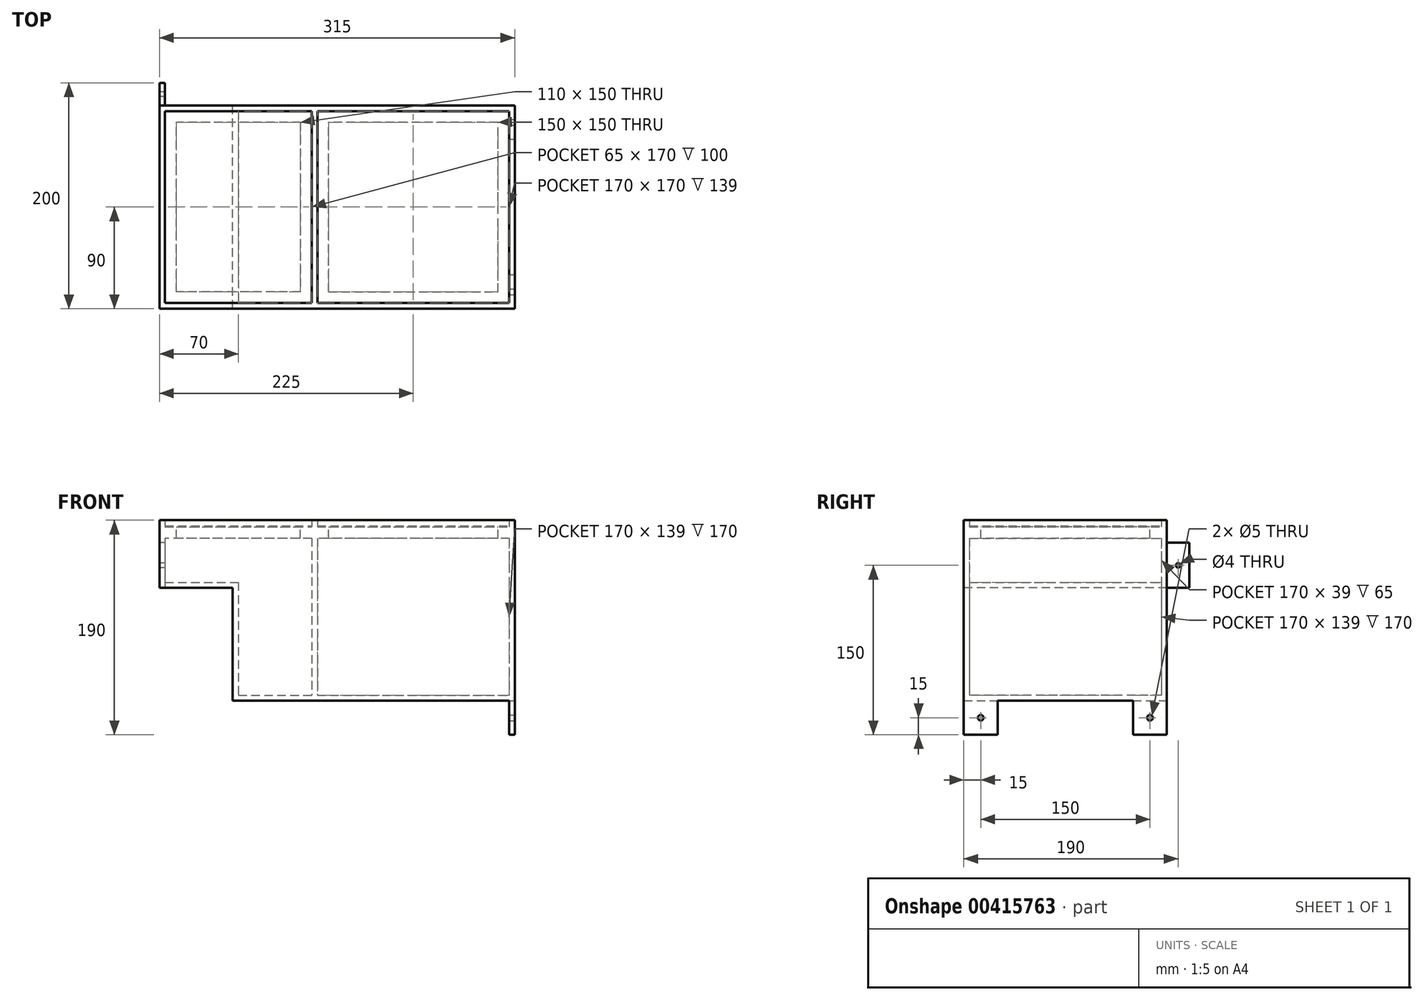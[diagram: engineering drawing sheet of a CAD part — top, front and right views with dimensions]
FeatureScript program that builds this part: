
annotation { "Feature Type Name" : "Feature", "Feature Type Description" : "" }
export const myFeature = defineFeature(function(context is Context, id is Id, definition is map)
    precondition{}
    {
        {
            var Q0;
            Q0=qCreatedBy(makeId("Top.planeOp"),FACE);
            var sketch = newSketch(context, id + "F0", { "sketchPlane" : qUnion([Q0])});
            skLineSegment(sketch, "E0.bottom", {"start": v(125, -90) * mm, "end": v(-125, -90) * mm});
            skLineSegment(sketch, "E0.top", {"start": v(125, 90) * mm, "end": v(-125, 90) * mm});
            skLineSegment(sketch, "E0.left", {"start": v(125, -90) * mm, "end": v(125, 90) * mm});
            skLineSegment(sketch, "E0.right", {"start": v(-125, -90) * mm, "end": v(-125, 90) * mm});
            skPoint(sketch, "E0.middle", {"position": v(0, 0) * mm});
            skLineSegment(sketch, "E1", {"start": v(-55, 90) * mm, "end": v(-55, -90) * mm});
            skLineSegment(sketch, "E2", {"start": v(-50, 90) * mm, "end": v(-50, -90) * mm});
            skLineSegment(sketch, "E3", {"start": v(-125, 85) * mm, "end": v(125, 85) * mm});
            skLineSegment(sketch, "E4", {"start": v(125, -85) * mm, "end": v(-125, -85) * mm});
            skLineSegment(sketch, "E5", {"start": v(120, 85) * mm, "end": v(120, -85) * mm});
            skLineSegment(sketch, "E6", {"start": v(-120, 85) * mm, "end": v(-120, -85) * mm});
            skSolve(sketch);
        }
        {
            var Q0;
            Q0 = qSketchRegion(id + "F0", true);
            var Q1;
            {var subQ0=sQuery(id+"F0.wireOp",EDGE,"E3");var subQ1=sQuery(id+"F0.wireOp",EDGE,"E1");var subQ2=makeQuery(id+"F0.imprint","INTERSECT",VERTEX,{"derivedFrom":[subQ1,subQ0]});Q1=makeQuery(id+"F0.imprint","IMPRINT",FACE,{"disambiguationData":[TD([[makeQuery(id+"F0.imprint","IMPRINT",EDGE,{"disambiguationData":[TD([[subQ2,-1.0]])],"derivedFrom":subQ1}),1.0]])]});}
            extrude(context, id + "F1", {"entities" : qUnion([Q0, Q1]), "depth" : 160 * mm});
        }
        {
            var Q0;
            {var subQ5=sQuery(id+"F0.wireOp",EDGE,"E6");Q0=makeQuery(id+"F0.imprint","IMPRINT",FACE,{"disambiguationData":[TD([[makeQuery(id+"F0.imprint","IMPRINT",EDGE,{"derivedFrom":subQ5}),1.0]])]});}
            var Q1;
            {var subQ5=sQuery(id+"F0.wireOp",EDGE,"E5");Q1=makeQuery(id+"F0.imprint","IMPRINT",FACE,{"disambiguationData":[TD([[makeQuery(id+"F0.imprint","IMPRINT",EDGE,{"derivedFrom":subQ5}),-1.0]])]});}
            extrude(context, id + "F2", {"entities" : qUnion([Q0, Q1]), "operationType" : NewBodyOperationType.ADD, "depth" : 5 * mm});
        }
        {
            var Q0;
            Q0=makeQuery(id+"F1.opExtrude","SWEPT_FACE",FACE,{"disambiguationData":[OSD([sQuery(id+"F0.wireOp",EDGE,"E0.right")])]});
            var sketch = newSketch(context, id + "F3", { "sketchPlane" : qUnion([Q0])});
            skLineSegment(sketch, "E7.bottom", {"start": v(-90, 160) * mm, "end": v(90, 160) * mm});
            skLineSegment(sketch, "E7.top", {"start": v(-90, 100) * mm, "end": v(90, 100) * mm});
            skLineSegment(sketch, "E7.left", {"start": v(-90, 160) * mm, "end": v(-90, 100) * mm});
            skLineSegment(sketch, "E7.right", {"start": v(90, 160) * mm, "end": v(90, 100) * mm});
            skLineSegment(sketch, "E8", {"start": v(90, 155) * mm, "end": v(-90, 155) * mm});
            skLineSegment(sketch, "E9", {"start": v(-90, 105) * mm, "end": v(90, 105) * mm});
            skLineSegment(sketch, "E10", {"start": v(85, 155) * mm, "end": v(85, 105) * mm});
            skLineSegment(sketch, "E11", {"start": v(-85, 155) * mm, "end": v(-85, 105) * mm});
            skSolve(sketch);
        }
        {
            var Q0;
            Q0 = qSketchRegion(id + "F3", true);
            var Q1;
            {var subQ0=sQuery(id+"F3.wireOp",EDGE,"E10");Q1=makeQuery(id+"F3.imprint","IMPRINT",FACE,{"disambiguationData":[TD([[makeQuery(id+"F3.imprint","IMPRINT",EDGE,{"derivedFrom":subQ0}),-1.0]])]});}
            extrude(context, id + "F4", {"entities" : qUnion([Q0, Q1]), "operationType" : NewBodyOperationType.ADD, "depth" : 65 * mm});
        }
        {
            var Q0;
            {var subQ0=sQuery(id+"F3.wireOp",EDGE,"E10");Q0=makeQuery(id+"F3.imprint","IMPRINT",FACE,{"disambiguationData":[TD([[makeQuery(id+"F3.imprint","IMPRINT",EDGE,{"derivedFrom":subQ0}),-1.0]])]});}
            extrude(context, id + "F5", {"entities" : qUnion([Q0]), "operationType" : NewBodyOperationType.REMOVE, "depth" : 60 * mm});
        }
        {
            var Q0;
            {var subQ0=sQuery(id+"F3.wireOp",EDGE,"E10");Q0=makeQuery(id+"F3.imprint","IMPRINT",FACE,{"disambiguationData":[TD([[makeQuery(id+"F3.imprint","IMPRINT",EDGE,{"derivedFrom":subQ0}),-1.0]])]});}
            extrude(context, id + "F6", {"entities" : qUnion([Q0]), "operationType" : NewBodyOperationType.REMOVE, "oppositeDirection" : true, "depth" : 6 * mm});
        }
        {
            var Q0;
            {var subQ0=sQuery(id+"F0.wireOp",EDGE,"E6");Q0=makeQuery(id+"F6.boolean.opBoolean","SPLIT",FACE,{"disambiguationData":[TD([makeQuery(id+"F4.opExtrude","SWEPT_FACE",FACE,{"disambiguationData":[OSD([sQuery(id+"F3.wireOp",EDGE,"E7.bottom")])]})])],"derivedFrom":makeQuery(id+"F1.opExtrude","SWEPT_FACE",FACE,{"disambiguationData":[OSD([subQ0])]})});}
            extrude(context, id + "F7", {"entities" : qUnion([Q0]), "operationType" : NewBodyOperationType.REMOVE, "oppositeDirection" : true, "depth" : 65 * mm});
        }
        {
            var Q0;
            Q0=makeQuery(id+"F4.opExtrude","CAP_FACE",FACE,{"disambiguationData":[OSD([sQuery(id+"F3.wireOp",EDGE,"E7.bottom"),sQuery(id+"F3.wireOp",EDGE,"E7.top"),sQuery(id+"F3.wireOp",EDGE,"E7.left"),sQuery(id+"F3.wireOp",EDGE,"E7.right")])],"isStart":false});
            var sketch = newSketch(context, id + "F8", { "sketchPlane" : qUnion([Q0])});
            skLineSegment(sketch, "E12.bottom", {"start": v(-90, 100) * mm, "end": v(-110, 100) * mm});
            skLineSegment(sketch, "E12.top", {"start": v(-90, 140) * mm, "end": v(-110, 140) * mm});
            skLineSegment(sketch, "E12.left", {"start": v(-90, 100) * mm, "end": v(-90, 140) * mm});
            skLineSegment(sketch, "E12.right", {"start": v(-110, 100) * mm, "end": v(-110, 140) * mm});
            skLineSegment(sketch, "E13", {"start": v(-110, 120) * mm, "end": v(-90, 120) * mm, "construction": true});
            skCircle(sketch, "E14", {"center": v(-100, 120) * mm, "radius": 2 * mm});
            skSolve(sketch);
        }
        {
            var Q0;
            Q0 = qSketchRegion(id + "F8", true);
            extrude(context, id + "F9", {"entities" : qUnion([Q0]), "oppositeDirection" : true, "depth" : 5 * mm});
        }
        {
            var Q0;
            Q0=makeQuery(id+"F1.opExtrude","SWEPT_FACE",FACE,{"disambiguationData":[OSD([sQuery(id+"F0.wireOp",EDGE,"E0.left")])]});
            var sketch = newSketch(context, id + "F10", { "sketchPlane" : qUnion([Q0])});
            skLineSegment(sketch, "E15.bottom", {"start": v(-90, 0) * mm, "end": v(-60, 0) * mm});
            skLineSegment(sketch, "E15.top", {"start": v(-90, -30) * mm, "end": v(-60, -30) * mm});
            skLineSegment(sketch, "E15.left", {"start": v(-90, 0) * mm, "end": v(-90, -30) * mm});
            skLineSegment(sketch, "E15.right", {"start": v(-60, 0) * mm, "end": v(-60, -30) * mm});
            skLineSegment(sketch, "E16.bottom", {"start": v(90, 0) * mm, "end": v(60, 0) * mm});
            skLineSegment(sketch, "E16.top", {"start": v(90, -30) * mm, "end": v(60, -30) * mm});
            skLineSegment(sketch, "E16.left", {"start": v(90, 0) * mm, "end": v(90, -30) * mm});
            skLineSegment(sketch, "E16.right", {"start": v(60, 0) * mm, "end": v(60, -30) * mm});
            skLineSegment(sketch, "E17", {"start": v(-60, -15) * mm, "end": v(-90, -15) * mm, "construction": true});
            skLineSegment(sketch, "E18", {"start": v(90, -15) * mm, "end": v(60, -15) * mm, "construction": true});
            skCircle(sketch, "E19", {"center": v(-75, -15) * mm, "radius": 2.5 * mm});
            skCircle(sketch, "E20", {"center": v(75, -15) * mm, "radius": 2.5 * mm});
            skSolve(sketch);
        }
        {
            var Q0;
            Q0 = qSketchRegion(id + "F10", true);
            extrude(context, id + "F11", {"entities" : qUnion([Q0]), "operationType" : NewBodyOperationType.ADD, "oppositeDirection" : true, "depth" : 5 * mm});
        }
        {
            var Q0;
            {var subQ0=sQuery(id+"F0.wireOp",EDGE,"E3");Q0=makeQuery(id+"F1.opExtrude","SWEPT_FACE",FACE,{"disambiguationData":[OSD([subQ0]),TDD([makeQuery(id+"F0.imprint","IMPRINT",EDGE,{"disambiguationData":[TD([[makeQuery(id+"F0.imprint","INTERSECT",VERTEX,{"derivedFrom":[subQ0,sQuery(id+"F0.wireOp",EDGE,"E5")]}),1.0]])],"derivedFrom":subQ0})])]});}
            var sketch = newSketch(context, id + "F12", { "sketchPlane" : qUnion([Q0])});
            skLineSegment(sketch, "E21", {"start": v(-50, 154) * mm, "end": v(120, 154) * mm});
            skLineSegment(sketch, "E22", {"start": v(120, 144) * mm, "end": v(-50, 144) * mm});
            skSolve(sketch);
        }
        {
            var Q0;
            {var subQ0=sQuery(id+"F12.wireOp",EDGE,"E21");Q0=makeQuery(id+"F12.imprint","IMPRINT",FACE,{"disambiguationData":[TD([[makeQuery(id+"F12.imprint","IMPRINT",EDGE,{"derivedFrom":subQ0}),-1.0]])]});}
            extrude(context, id + "F13", {"entities" : qUnion([Q0]), "operationType" : NewBodyOperationType.ADD, "depth" : 170 * mm});
        }
        {
            var Q0;
            Q0=makeQuery(id+"F13.opExtrude","SWEPT_FACE",FACE,{"disambiguationData":[OSD([sQuery(id+"F12.wireOp",EDGE,"E21")])]});
            var sketch = newSketch(context, id + "F14", { "sketchPlane" : qUnion([Q0])});
            skLineSegment(sketch, "E23", {"start": v(-50, 75) * mm, "end": v(120, 75) * mm});
            skLineSegment(sketch, "E24", {"start": v(120, -75) * mm, "end": v(-50, -75) * mm});
            skLineSegment(sketch, "E25", {"start": v(110, 75) * mm, "end": v(110, -75) * mm});
            skLineSegment(sketch, "E26", {"start": v(-40, 75) * mm, "end": v(-40, -75) * mm});
            skSolve(sketch);
        }
        {
            var Q0;
            {var subQ0=sQuery(id+"F14.wireOp",EDGE,"E25");Q0=makeQuery(id+"F14.imprint","IMPRINT",FACE,{"disambiguationData":[TD([[makeQuery(id+"F14.imprint","IMPRINT",EDGE,{"derivedFrom":subQ0}),-1.0]])]});}
            extrude(context, id + "F15", {"entities" : qUnion([Q0]), "operationType" : NewBodyOperationType.REMOVE, "oppositeDirection" : true, "depth" : 11 * mm});
        }
        {
            var Q0;
            {var subQ0=sQuery(id+"F0.wireOp",EDGE,"E6");var subQ1=sQuery(id+"F0.wireOp",EDGE,"E3");var subQ2=sQuery(id+"F3.wireOp",EDGE,"E11");Q0=makeQuery(id+"F7.boolean.opBoolean","MERGE",FACE,{"derivedFrom":[makeQuery(id+"F6.boolean.opBoolean","MERGE",FACE,{"derivedFrom":[makeQuery(id+"F1.opExtrude","SWEPT_FACE",FACE,{"disambiguationData":[OSD([subQ1]),TDD([makeQuery(id+"F0.imprint","IMPRINT",EDGE,{"disambiguationData":[TD([[makeQuery(id+"F0.imprint","INTERSECT",VERTEX,{"derivedFrom":[subQ1,subQ0]}),-1.0]])],"derivedFrom":subQ1})])]}),makeQuery(id+"F5.boolean.opBoolean","COPY",FACE,{"derivedFrom":makeQuery(id+"F5.opExtrude","SWEPT_FACE",FACE,{"disambiguationData":[OSD([subQ2])]})}),makeQuery(id+"F6.opExtrude","SWEPT_FACE",FACE,{"disambiguationData":[OSD([subQ2])]})]}),makeQuery(id+"F7.opExtrude","SWEPT_FACE",FACE,{"disambiguationData":[OSD([subQ1,subQ0])]})]});}
            var sketch = newSketch(context, id + "F16", { "sketchPlane" : qUnion([Q0])});
            skLineSegment(sketch, "E27", {"start": v(-185, 154) * mm, "end": v(-55, 154) * mm});
            skLineSegment(sketch, "E28", {"start": v(-55, 144) * mm, "end": v(-185, 144) * mm});
            skSolve(sketch);
        }
        {
            var Q0;
            {var subQ0=sQuery(id+"F16.wireOp",EDGE,"E27");Q0=makeQuery(id+"F16.imprint","IMPRINT",FACE,{"disambiguationData":[TD([[makeQuery(id+"F16.imprint","IMPRINT",EDGE,{"derivedFrom":subQ0}),-1.0]])]});}
            extrude(context, id + "F17", {"entities" : qUnion([Q0]), "operationType" : NewBodyOperationType.ADD, "depth" : 170 * mm});
        }
        {
            var Q0;
            Q0=makeQuery(id+"F17.opExtrude","SWEPT_FACE",FACE,{"disambiguationData":[OSD([sQuery(id+"F16.wireOp",EDGE,"E27")])]});
            var sketch = newSketch(context, id + "F18", { "sketchPlane" : qUnion([Q0])});
            skLineSegment(sketch, "E29", {"start": v(-185, 75) * mm, "end": v(-55, 75) * mm});
            skLineSegment(sketch, "E30", {"start": v(-185, -75) * mm, "end": v(-55, -75) * mm});
            skLineSegment(sketch, "E31", {"start": v(-65, -75) * mm, "end": v(-65, 75) * mm});
            skLineSegment(sketch, "E32", {"start": v(-175, 75) * mm, "end": v(-175, -75) * mm});
            skSolve(sketch);
        }
        {
            var Q0;
            {var subQ0=sQuery(id+"F18.wireOp",EDGE,"E31");Q0=makeQuery(id+"F18.imprint","IMPRINT",FACE,{"disambiguationData":[TD([[makeQuery(id+"F18.imprint","IMPRINT",EDGE,{"derivedFrom":subQ0}),1.0]])]});}
            extrude(context, id + "F19", {"entities" : qUnion([Q0]), "operationType" : NewBodyOperationType.REMOVE, "oppositeDirection" : true, "depth" : 11 * mm});
        }
        {
            var Q0;
            {var subQ0=sQuery(id+"F0.wireOp",EDGE,"E5");var subQ2=sQuery(id+"F0.wireOp",EDGE,"E3");Q0=makeQuery(id+"F13.boolean.opBoolean","SPLIT",FACE,{"disambiguationData":[TD([makeQuery(id+"F4.opExtrude","SWEPT_FACE",FACE,{"disambiguationData":[OSD([sQuery(id+"F3.wireOp",EDGE,"E7.bottom")])]})])],"derivedFrom":makeQuery(id+"F1.opExtrude","SWEPT_FACE",FACE,{"disambiguationData":[OSD([subQ2]),TDD([makeQuery(id+"F0.imprint","IMPRINT",EDGE,{"disambiguationData":[TD([[makeQuery(id+"F0.imprint","INTERSECT",VERTEX,{"derivedFrom":[subQ2,subQ0]}),1.0]])],"derivedFrom":subQ2})])]})});}
            var sketch = newSketch(context, id + "F20", { "sketchPlane" : qUnion([Q0])});
            skLineSegment(sketch, "E33.bottom", {"start": v(-50, 160) * mm, "end": v(120, 160) * mm});
            skLineSegment(sketch, "E33.top", {"start": v(-50, 155) * mm, "end": v(120, 155) * mm});
            skLineSegment(sketch, "E33.left", {"start": v(-50, 160) * mm, "end": v(-50, 155) * mm});
            skLineSegment(sketch, "E33.right", {"start": v(120, 160) * mm, "end": v(120, 155) * mm});
            skSolve(sketch);
        }
        {
            var Q0;
            Q0=makeQuery(id+"F20.imprint","IMPRINT",FACE,{"disambiguationData":[TD([[makeQuery(id+"F20.imprint","IMPRINT",EDGE,{"derivedFrom":sQuery(id+"F20.wireOp",EDGE,"E33.bottom")}),-1.0]])]});
            extrude(context, id + "F21", {"entities" : qUnion([Q0]), "depth" : 170 * mm});
        }
        {
            var Q0;
            {var subQ0=sQuery(id+"F3.wireOp",EDGE,"E11");var subQ2=sQuery(id+"F0.wireOp",EDGE,"E6");var subQ3=sQuery(id+"F0.wireOp",EDGE,"E3");Q0=makeQuery(id+"F17.boolean.opBoolean","SPLIT",FACE,{"disambiguationData":[TD([makeQuery(id+"F4.opExtrude","SWEPT_FACE",FACE,{"disambiguationData":[OSD([sQuery(id+"F3.wireOp",EDGE,"E7.bottom")])]})])],"derivedFrom":makeQuery(id+"F7.boolean.opBoolean","MERGE",FACE,{"derivedFrom":[makeQuery(id+"F6.boolean.opBoolean","MERGE",FACE,{"derivedFrom":[makeQuery(id+"F1.opExtrude","SWEPT_FACE",FACE,{"disambiguationData":[OSD([subQ3]),TDD([makeQuery(id+"F0.imprint","IMPRINT",EDGE,{"disambiguationData":[TD([[makeQuery(id+"F0.imprint","INTERSECT",VERTEX,{"derivedFrom":[subQ3,subQ2]}),-1.0]])],"derivedFrom":subQ3})])]}),makeQuery(id+"F5.boolean.opBoolean","COPY",FACE,{"derivedFrom":makeQuery(id+"F5.opExtrude","SWEPT_FACE",FACE,{"disambiguationData":[OSD([subQ0])]})}),makeQuery(id+"F6.opExtrude","SWEPT_FACE",FACE,{"disambiguationData":[OSD([subQ0])]})]}),makeQuery(id+"F7.opExtrude","SWEPT_FACE",FACE,{"disambiguationData":[OSD([subQ3,subQ2])]})]})});}
            var sketch = newSketch(context, id + "F22", { "sketchPlane" : qUnion([Q0])});
            skLineSegment(sketch, "E34.bottom", {"start": v(-185, 160) * mm, "end": v(-55, 160) * mm});
            skLineSegment(sketch, "E34.top", {"start": v(-185, 155) * mm, "end": v(-55, 155) * mm});
            skLineSegment(sketch, "E34.left", {"start": v(-185, 160) * mm, "end": v(-185, 155) * mm});
            skLineSegment(sketch, "E34.right", {"start": v(-55, 160) * mm, "end": v(-55, 155) * mm});
            skSolve(sketch);
        }
        {
            var Q0;
            Q0=makeQuery(id+"F22.imprint","IMPRINT",FACE,{"disambiguationData":[TD([[makeQuery(id+"F22.imprint","IMPRINT",EDGE,{"derivedFrom":sQuery(id+"F22.wireOp",EDGE,"E34.bottom")}),-1.0]])]});
            extrude(context, id + "F23", {"entities" : qUnion([Q0]), "depth" : 170 * mm});
        }
    });
